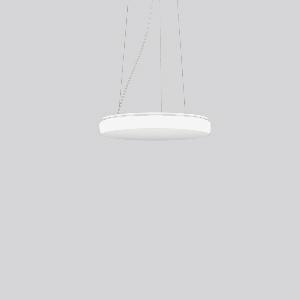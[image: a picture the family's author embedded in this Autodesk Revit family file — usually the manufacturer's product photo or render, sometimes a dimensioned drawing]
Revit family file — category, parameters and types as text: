
# Revit family: flat_polymero_kreis_slim_312090_002_2_76_c69c
name_source: partatom
category: Lighting Fixtures
units: mm (PartAtom-declared; Revit-internal decimal feet)

## family parameters
Cut with Voids When Loaded = No
Host = Face
Light Source = No
Part Type = Normal
Room Calculation Point = No
Round Connector Dimension = Use Diameter
Shared = No

## types (1)
- FLAT POLYMERO KREIS SLIM (1 x LED Modul 830, 2000 lm, 3000)
    Apparent Load = 19 VA
    CIE Flux Codes = 44 76 94 92 100
    Color Rendering = 80
    Color Temperature = 3000
    Default Elevation = 1800 mm
    Description = Series: FLAT POLYMERO KREIS SLIM
Decorative round LED pendant luminaire. Base and canopy: metal, powder-coated, white. Canopy Ø 205 mm, h 35 mm. Diffuser made of plastic (polycarbonate), opal, shockproof. Diffuser fastening: patented push system. Homogeneous and smooth light distribution. Suitable for pendant. 3-point steel cable suspension, steplessly adjustable. Special lengths available on request. TouchDim sensor capable. Light and/or presence sensors can be integrated. 
Colour: white
Diameter: 460 mm
Height: 68 mm
Suspension length: 200-1300 mm
Lamp: LED
Socket: without socket
Colour temperature: 3000K
Colour rendering index (CRI): 83
System power: 19 W
Rated luminous flux: 2000 lm
Luminous efficiency: 105 lm/W
Control gear: AC power, DALI dimmable
Protection class: I
Type of protection: IP 40
    Height = 68 mm
    Lamp = 1 x LED Modul 830
    Lamp Light Flux = 2000 lm
    Lamp count = 1
    Length = 460 mm
    Lifetime = 50000 h
    Luminous efficacy = 105 lm/W
    Manufacturer = RZB
    ModVariant = No
    Model = 312090.002.2.76
    Mounting Place = Ceiling
    Mounting Type = Pendant
    Number of Poles = 1
    OnlyDefault = Yes
    Power Factor = 1
    Product Name = FLAT POLYMERO KREIS SLIM
    Product group = Pendant luminaires
    ProductGroupID = 902
    Protection Class = Protection class I
    Protection Degree = IP 40
    RLX_Detail_Level = 1
    RLX_Emergency_Light_Flux = 0 lm
    RLX_Emergency_Type = 0
    RLX_Emergency_Type_DB = No
    RlxData = <blob elided: 58857 chars, md5=47abe547>
    Socket = socket
    Standby Power = 0 W
    System Light Flux = 2000 lm
    System Power = 19 W
    Type Comments = Product without accessories
    Type Image = 312090.002.jpg
    URL = http://relux.com
    VarID = ---
    Voltage = 230 V
    Voltage Range = 220-240 V
    Weight = 0.00 kg
    Width = 0 mm  [stored 0 ft]

note: [stored X ft] marks values corroborated as IEEE doubles in the binary element streams (Revit-internal decimal feet)

## geometry (parser evidence)
native form markers: Blend x4, Sweep x13
no freeform markers — native parametric forms only
